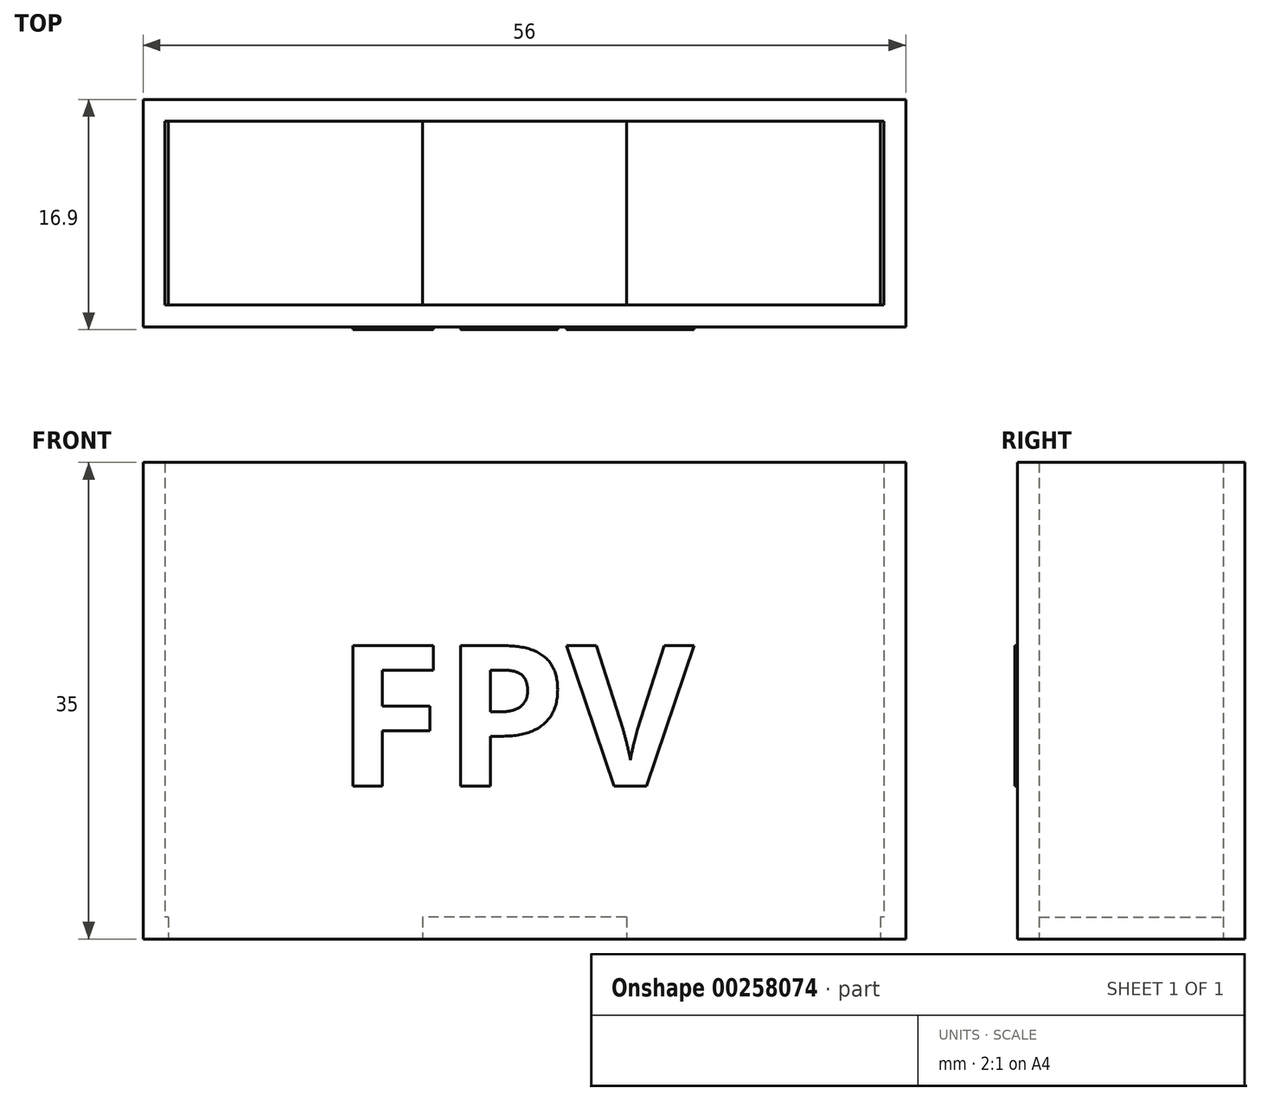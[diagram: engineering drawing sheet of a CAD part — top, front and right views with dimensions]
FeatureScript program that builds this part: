
annotation { "Feature Type Name" : "Feature", "Feature Type Description" : "" }
export const myFeature = defineFeature(function(context is Context, id is Id, definition is map)
    precondition{}
    {
        {
            var Q0;
            Q0=qCreatedBy(makeId("Top.planeOp"),FACE);
            var sketch = newSketch(context, id + "F0", { "sketchPlane" : qUnion([Q0])});
            skLineSegment(sketch, "E0.bottom", {"start": v(28, -8.35) * mm, "end": v(-28, -8.35) * mm});
            skLineSegment(sketch, "E0.top", {"start": v(28, 8.35) * mm, "end": v(-28, 8.35) * mm});
            skLineSegment(sketch, "E0.left", {"start": v(28, -8.35) * mm, "end": v(28, 8.35) * mm});
            skLineSegment(sketch, "E0.right", {"start": v(-28, -8.35) * mm, "end": v(-28, 8.35) * mm});
            skPoint(sketch, "E0.middle", {"position": v(0, 0) * mm});
            skSolve(sketch);
        }
        {
            var Q0;
            Q0 = qSketchRegion(id + "F0", true);
            extrude(context, id + "F1", {"entities" : qUnion([Q0]), "depth" : 35 * mm});
        }
        {
            var Q0;
            Q0=makeQuery(id+"F1.opExtrude","CAP_FACE",FACE,{"disambiguationData":[OSD([sQuery(id+"F0.wireOp",EDGE,"E0.bottom"),sQuery(id+"F0.wireOp",EDGE,"E0.top"),sQuery(id+"F0.wireOp",EDGE,"E0.left"),sQuery(id+"F0.wireOp",EDGE,"E0.right")])],"isStart":false});
            shell(context, id + "F2", {"entities" : qUnion([Q0]), "thickness" : 1.6 * mm});
        }
        {
            var Q0;
            Q0=makeQuery(id+"F1.opExtrude","CAP_FACE",FACE,{"disambiguationData":[OSD([sQuery(id+"F0.wireOp",EDGE,"E0.bottom"),sQuery(id+"F0.wireOp",EDGE,"E0.top"),sQuery(id+"F0.wireOp",EDGE,"E0.left"),sQuery(id+"F0.wireOp",EDGE,"E0.right")])],"isStart":true});
            var sketch = newSketch(context, id + "F3", { "sketchPlane" : qUnion([Q0])});
            skLineSegment(sketch, "E1.bottom", {"start": v(7.5, -8.35) * mm, "end": v(-7.5, -8.35) * mm, "construction": true});
            skLineSegment(sketch, "E1.top", {"start": v(7.5, 8.35) * mm, "end": v(-7.5, 8.35) * mm, "construction": true});
            skLineSegment(sketch, "E1.left", {"start": v(7.5, -8.35) * mm, "end": v(7.5, 8.35) * mm, "construction": true});
            skLineSegment(sketch, "E1.right", {"start": v(-7.5, -8.35) * mm, "end": v(-7.5, 8.35) * mm, "construction": true});
            skPoint(sketch, "E1.middle", {"position": v(0, 0) * mm});
            skLineSegment(sketch, "E2.bottom", {"start": v(26.15, -6.75) * mm, "end": v(-26.15, -6.75) * mm, "construction": true});
            skLineSegment(sketch, "E2.top", {"start": v(26.15, 6.75) * mm, "end": v(-26.15, 6.75) * mm, "construction": true});
            skLineSegment(sketch, "E2.left", {"start": v(26.15, -6.75) * mm, "end": v(26.15, 6.75) * mm, "construction": true});
            skLineSegment(sketch, "E2.right", {"start": v(-26.15, -6.75) * mm, "end": v(-26.15, 6.75) * mm, "construction": true});
            skLineSegment(sketch, "E3.bottom", {"start": v(-26.15, 6.75) * mm, "end": v(-7.5, 6.75) * mm});
            skLineSegment(sketch, "E3.top", {"start": v(-26.15, -6.75) * mm, "end": v(-7.5, -6.75) * mm});
            skLineSegment(sketch, "E3.left", {"start": v(-26.15, 6.75) * mm, "end": v(-26.15, -6.75) * mm});
            skLineSegment(sketch, "E3.right", {"start": v(-7.5, 6.75) * mm, "end": v(-7.5, -6.75) * mm});
            skLineSegment(sketch, "E4.bottom", {"start": v(26.15, 6.75) * mm, "end": v(7.5, 6.75) * mm});
            skLineSegment(sketch, "E4.top", {"start": v(26.15, -6.75) * mm, "end": v(7.5, -6.75) * mm});
            skLineSegment(sketch, "E4.left", {"start": v(26.15, 6.75) * mm, "end": v(26.15, -6.75) * mm});
            skLineSegment(sketch, "E4.right", {"start": v(7.5, 6.75) * mm, "end": v(7.5, -6.75) * mm});
            skSolve(sketch);
        }
        {
            var Q0;
            Q0=makeQuery(id+"F3.imprint","IMPRINT",FACE,{"disambiguationData":[TD([[makeQuery(id+"F3.imprint","IMPRINT",EDGE,{"derivedFrom":sQuery(id+"F3.wireOp",EDGE,"E4.bottom")}),1.0]])]});
            var Q1;
            Q1=makeQuery(id+"F3.imprint","IMPRINT",FACE,{"disambiguationData":[TD([[makeQuery(id+"F3.imprint","IMPRINT",EDGE,{"derivedFrom":sQuery(id+"F3.wireOp",EDGE,"E3.bottom")}),-1.0]])]});
            extrude(context, id + "F4", {"entities" : qUnion([Q0, Q1]), "operationType" : NewBodyOperationType.REMOVE, "endBound" : BoundingType.UP_TO_NEXT, "oppositeDirection" : true, "depth" : 25 * mm});
        }
        {
            var Q0;
            Q0=makeQuery(id+"F1.opExtrude","SWEPT_FACE",FACE,{"disambiguationData":[OSD([sQuery(id+"F0.wireOp",EDGE,"E0.bottom")])]});
            var sketch = newSketch(context, id + "F5", { "sketchPlane" : qUnion([Q0])});
            skText(sketch, "E5", { "text": "FPV", "fontName": "OpenSans-Bold.ttf"});
            const initialGuessF5  = {"E5": [-0.0139, 0.01123, 1, 0, 0.01039]};
            skSetInitialGuess(sketch, initialGuessF5);
            skSolve(sketch);
        }
        {
            var Q0;
            Q0 = qSketchRegion(id + "F5", true);
            extrude(context, id + "F6", {"entities" : qUnion([Q0]), "operationType" : NewBodyOperationType.ADD, "depth" : 0.2 * mm});
        }
    });
